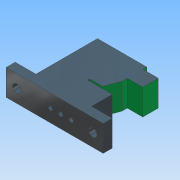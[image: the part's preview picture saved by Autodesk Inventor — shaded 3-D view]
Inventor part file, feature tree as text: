
AUTODESK INVENTOR PART (.ipt)
format: ipt  version: 2016 (Build 200138000, 138)  size: 124,416 bytes
history: native  units: mm
features: hole x2, extrude x1
ambient origin geometry x8: Origin, YZ Plane, XZ Plane, XY Plane, X Axis, Y Axis, Z Axis, Center Point
bodies: Volumenkörper1 (feature_tree)
feature tree (3):
  extrude  "Extrusion1"  Depth=27.3mm
  hole  "Bohrung1"  [1 undecoded]
  hole  "Bohrung2"  [1 undecoded]
note: 2 required parameter values undecoded (feature->parameter linkage not recoverable at this tier; creation-order binding heuristic only, values carry confidence <= 0.55)
